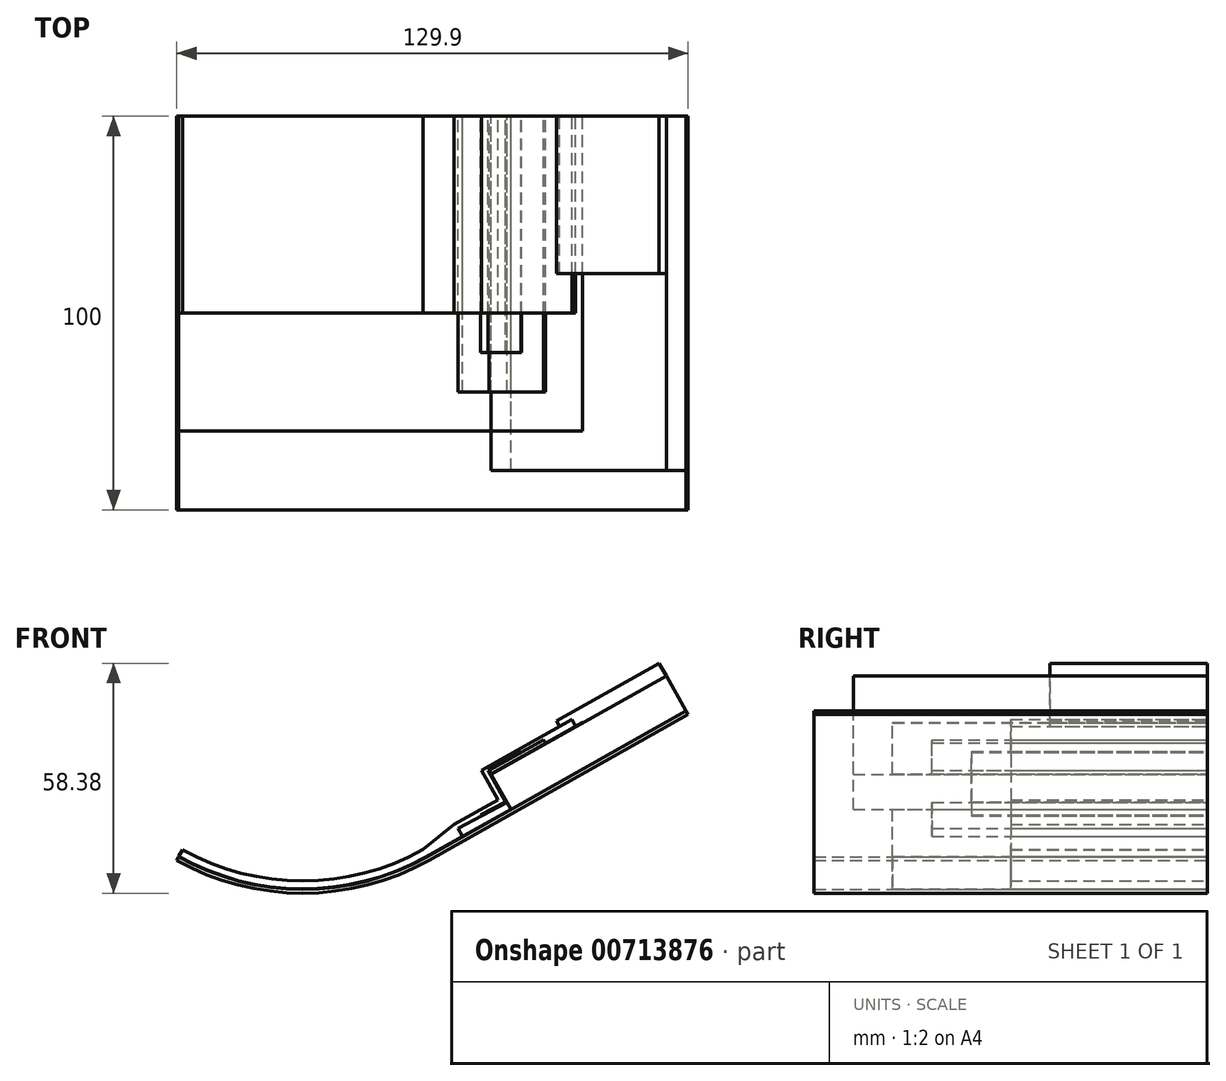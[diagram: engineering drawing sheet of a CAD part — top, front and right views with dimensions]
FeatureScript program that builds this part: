
annotation { "Feature Type Name" : "Feature", "Feature Type Description" : "" }
export const myFeature = defineFeature(function(context is Context, id is Id, definition is map)
    precondition{}
    {
        {
            var Q0;
            Q0=qCreatedBy(makeId("Front.planeOp"),FACE);
            var sketch = newSketch(context, id + "F0", { "sketchPlane" : qUnion([Q0])});
            skLineSegment(sketch, "E0", {"start": v(29.52, 14.22) * mm, "end": v(95.32, 51.26) * mm});
            skArc(sketch, "E1", {"start": v(-33.6, 14.22) * mm, "mid": v(-2.04, 6) * mm, "end": v(29.52, 14.22) * mm});
            skLineSegment(sketch, "E2.0", {"start": v(30.01, 13.35) * mm, "end": v(95.81, 50.38) * mm});
            skArc(sketch, "E2.1", {"start": v(-34.09, 13.35) * mm, "mid": v(-2.04, 5) * mm, "end": v(30.01, 13.35) * mm});
            skLineSegment(sketch, "E3", {"start": v(95.32, 51.26) * mm, "end": v(95.81, 50.38) * mm});
            skLineSegment(sketch, "E4", {"start": v(50.85, 26.22) * mm, "end": v(45.83, 35.14) * mm});
            skLineSegment(sketch, "E5", {"start": v(45.83, 35.14) * mm, "end": v(90.3, 60.17) * mm});
            skLineSegment(sketch, "E6", {"start": v(90.3, 60.17) * mm, "end": v(95.32, 51.26) * mm});
            skArc(sketch, "E7.0", {"start": v(-33.55, 14.3) * mm, "mid": v(-2.27, 6.1) * mm, "end": v(29.07, 14.08) * mm});
            skArc(sketch, "E8.0", {"start": v(-32.58, 16.05) * mm, "mid": v(-2.04, 8.1) * mm, "end": v(28.5, 16.06) * mm});
            skLineSegment(sketch, "E9", {"start": v(29.07, 14.08) * mm, "end": v(50.8, 26.31) * mm});
            skLineSegment(sketch, "E10", {"start": v(49.79, 28.1) * mm, "end": v(37.4, 21.41) * mm});
            skLineSegment(sketch, "E11", {"start": v(37.4, 21.41) * mm, "end": v(38.5, 19.4) * mm});
            skLineSegment(sketch, "E12", {"start": v(-32.58, 16.05) * mm, "end": v(-34.09, 13.35) * mm});
            skLineSegment(sketch, "E13", {"start": v(45.83, 35.14) * mm, "end": v(45.74, 35.29) * mm});
            skLineSegment(sketch, "E14", {"start": v(45.74, 35.29) * mm, "end": v(68.97, 48.36) * mm});
            skLineSegment(sketch, "E15", {"start": v(68.97, 48.36) * mm, "end": v(69.05, 48.21) * mm});
            skLineSegment(sketch, "E16", {"start": v(45.74, 35.29) * mm, "end": v(45.25, 36.17) * mm});
            skLineSegment(sketch, "E17", {"start": v(45.25, 36.17) * mm, "end": v(59.14, 44) * mm});
            skLineSegment(sketch, "E18", {"start": v(59.14, 44) * mm, "end": v(59.64, 43.1) * mm});
            skLineSegment(sketch, "E19", {"start": v(53.4, 40.95) * mm, "end": v(53.49, 40.8) * mm});
            skLineSegment(sketch, "E20", {"start": v(53.4, 40.95) * mm, "end": v(44.95, 36.2) * mm});
            skLineSegment(sketch, "E21", {"start": v(44.95, 36.2) * mm, "end": v(49.45, 28.2) * mm});
            skLineSegment(sketch, "E22", {"start": v(49.45, 28.2) * mm, "end": v(43.13, 24.83) * mm});
            skLineSegment(sketch, "E23", {"start": v(43.13, 24.83) * mm, "end": v(43.26, 24.58) * mm});
            skLineSegment(sketch, "E24", {"start": v(67.28, 47.4) * mm, "end": v(66.3, 49.12) * mm});
            skLineSegment(sketch, "E25", {"start": v(66.3, 49.12) * mm, "end": v(43.36, 36.2) * mm});
            skLineSegment(sketch, "E26", {"start": v(43.36, 36.2) * mm, "end": v(47.57, 28.71) * mm});
            skLineSegment(sketch, "E27", {"start": v(47.57, 28.71) * mm, "end": v(36.4, 22.42) * mm});
            skLineSegment(sketch, "E28", {"start": v(36.4, 22.42) * mm, "end": v(28.5, 16.06) * mm});
            skLineSegment(sketch, "E29", {"start": v(90.3, 60.17) * mm, "end": v(88.5, 63.37) * mm});
            skLineSegment(sketch, "E30", {"start": v(88.5, 63.37) * mm, "end": v(62.44, 48.7) * mm});
            skLineSegment(sketch, "E31", {"start": v(62.44, 48.7) * mm, "end": v(63.2, 47.37) * mm});
            skSolve(sketch);
        }
        {
            var Q0;
            {var subQ0=sQuery(id+"F0.wireOp",EDGE,"E1");Q0=makeQuery(id+"F0.imprint","IMPRINT",FACE,{"disambiguationData":[TD([[makeQuery(id+"F0.imprint","IMPRINT",EDGE,{"derivedFrom":subQ0}),-1.0]])]});}
            extrude(context, id + "F1", {"entities" : qUnion([Q0]), "depth" : 100 * mm});
        }
        {
            var Q0;
            {var subQ7=sQuery(id+"F0.wireOp",EDGE,"E6");Q0=makeQuery(id+"F0.imprint","IMPRINT",FACE,{"disambiguationData":[TD([[makeQuery(id+"F0.imprint","IMPRINT",EDGE,{"derivedFrom":subQ7}),-1.0]])]});}
            extrude(context, id + "F2", {"entities" : qUnion([Q0]), "depth" : 90 * mm});
        }
        {
            var Q0;
            {var subQ6=sQuery(id+"F0.wireOp",EDGE,"E1");Q0=makeQuery(id+"F0.imprint","IMPRINT",FACE,{"disambiguationData":[TD([[makeQuery(id+"F0.imprint","IMPRINT",EDGE,{"derivedFrom":subQ6}),1.0]])]});}
            extrude(context, id + "F3", {"entities" : qUnion([Q0]), "depth" : 80 * mm});
        }
        {
            var Q0;
            {var subQ1=sQuery(id+"F0.wireOp",EDGE,"E13");Q0=makeQuery(id+"F0.imprint","IMPRINT",FACE,{"disambiguationData":[TD([[makeQuery(id+"F0.imprint","IMPRINT",EDGE,{"derivedFrom":subQ1}),-1.0]])]});}
            extrude(context, id + "F4", {"entities" : qUnion([Q0]), "depth" : 80 * mm});
        }
        {
            var Q0;
            {var subQ6=sQuery(id+"F0.wireOp",EDGE,"E11");Q0=makeQuery(id+"F0.imprint","IMPRINT",FACE,{"disambiguationData":[TD([[makeQuery(id+"F0.imprint","IMPRINT",EDGE,{"derivedFrom":subQ6}),1.0]])]});}
            var Q1;
            {var subQ3=sQuery(id+"F0.wireOp",EDGE,"E16");Q1=makeQuery(id+"F0.imprint","IMPRINT",FACE,{"disambiguationData":[TD([[makeQuery(id+"F0.imprint","IMPRINT",EDGE,{"derivedFrom":subQ3}),-1.0]])]});}
            extrude(context, id + "F5", {"entities" : qUnion([Q0, Q1]), "depth" : 70 * mm});
        }
        {
            var Q0;
            {var subQ5=sQuery(id+"F0.wireOp",EDGE,"E13");Q0=makeQuery(id+"F0.imprint","IMPRINT",FACE,{"disambiguationData":[TD([[makeQuery(id+"F0.imprint","IMPRINT",EDGE,{"derivedFrom":subQ5}),1.0]])]});}
            extrude(context, id + "F6", {"entities" : qUnion([Q0]), "depth" : 60 * mm});
        }
        {
            var Q0;
            {var subQ3=sQuery(id+"F0.wireOp",EDGE,"E7.0");Q0=makeQuery(id+"F0.imprint","IMPRINT",FACE,{"disambiguationData":[TD([[makeQuery(id+"F0.imprint","IMPRINT",EDGE,{"derivedFrom":subQ3}),1.0]])]});}
            extrude(context, id + "F7", {"entities" : qUnion([Q0]), "depth" : 50 * mm});
        }
        {
            var Q0;
            {var subQ1=sQuery(id+"F0.wireOp",EDGE,"E15");Q0=makeQuery(id+"F0.imprint","IMPRINT",FACE,{"disambiguationData":[TD([[makeQuery(id+"F0.imprint","IMPRINT",EDGE,{"derivedFrom":subQ1}),1.0]])]});}
            extrude(context, id + "F8", {"entities" : qUnion([Q0]), "depth" : 40 * mm});
        }
    });
